FCSTD DOCUMENT  (FreeCAD 0.19R)
Label: nozzle-carriage-v5
License: All rights reserved
LicenseURL: http://en.wikipedia.org/wiki/All_rights_reserved
objects: Sketcher::SketchObject×1, PartDesign::Body×1
note: 2 computed .brp shape members not serialized (recipe doc carries the construction recipe); baked Part::Feature solids carry a one-line shape summary decoded from their .brp

FEATURE [Sketcher::SketchObject] Sketch
  MapMode = 5
  Support = -> [XY_Plane]
  sketch-geometry (28):
    g0: LineSegment StartX=-27.5 StartY=-27.5 StartZ=0 EndX=27.5 EndY=-27.5 EndZ=0
    g1: LineSegment StartX=32.5 StartY=-22.5 StartZ=0 EndX=32.5 EndY=22.5 EndZ=0
    g2: LineSegment StartX=27.5 StartY=27.5 StartZ=0 EndX=-27.5 EndY=27.5 EndZ=0
    g3: LineSegment StartX=-32.5 StartY=22.5 StartZ=0 EndX=-32.5 EndY=-22.5 EndZ=0
    g4: ArcOfCircle CenterX=-27.5 CenterY=22.5 CenterZ=0 NormalX=0 NormalY=0 NormalZ=1 AngleXU=0 Radius=5 StartAngle=1.5708 EndAngle=3.14159
    g5: ArcOfCircle CenterX=27.5 CenterY=22.5 CenterZ=0 NormalX=0 NormalY=0 NormalZ=1 AngleXU=0 Radius=5 StartAngle=2e-16 EndAngle=1.5708
    g6: ArcOfCircle CenterX=27.5 CenterY=-22.5 CenterZ=0 NormalX=0 NormalY=0 NormalZ=1 AngleXU=0 Radius=5 StartAngle=4.71239 EndAngle=6.28319
    g7: ArcOfCircle CenterX=-27.5 CenterY=-22.5 CenterZ=0 NormalX=0 NormalY=0 NormalZ=1 AngleXU=0 Radius=5 StartAngle=3.14159 EndAngle=4.71239
    g8: LineSegment [constr] StartX=-32.5 StartY=20 StartZ=0 EndX=32.5 EndY=20 EndZ=0
    g9: Circle CenterX=-22.5 CenterY=20 CenterZ=0 NormalX=0 NormalY=0 NormalZ=1 AngleXU=0 Radius=3
    g10: Circle CenterX=22.5 CenterY=20 CenterZ=0 NormalX=0 NormalY=0 NormalZ=1 AngleXU=0 Radius=3
    g11: Circle CenterX=0 CenterY=-20 CenterZ=0 NormalX=0 NormalY=0 NormalZ=1 AngleXU=0 Radius=3
    g12: LineSegment [constr] StartX=-32.5 StartY=9.75 StartZ=0 EndX=32.5 EndY=9.75 EndZ=0
    g13: Circle CenterX=-12 CenterY=9.75 CenterZ=0 NormalX=0 NormalY=0 NormalZ=1 AngleXU=0 Radius=1.5
    g14: Circle CenterX=12 CenterY=9.75 CenterZ=0 NormalX=0 NormalY=0 NormalZ=1 AngleXU=0 Radius=1.5
    g15: LineSegment [constr] StartX=-32.5 StartY=-20 StartZ=0 EndX=32.5 EndY=-20 EndZ=0
    g16: Circle CenterX=-20.5 CenterY=-20 CenterZ=0 NormalX=0 NormalY=0 NormalZ=1 AngleXU=0 Radius=1.5
    g17: Circle CenterX=-13.5 CenterY=-20 CenterZ=0 NormalX=0 NormalY=0 NormalZ=1 AngleXU=0 Radius=1.5
    g18: Circle CenterX=-27.5 CenterY=-20 CenterZ=0 NormalX=0 NormalY=0 NormalZ=1 AngleXU=0 Radius=1.5
    g19: Circle CenterX=13.5 CenterY=-20 CenterZ=0 NormalX=0 NormalY=0 NormalZ=1 AngleXU=0 Radius=1.5
    g20: Circle CenterX=20.5 CenterY=-20 CenterZ=0 NormalX=0 NormalY=0 NormalZ=1 AngleXU=0 Radius=1.5
    g21: Circle CenterX=27.5 CenterY=-20 CenterZ=0 NormalX=0 NormalY=0 NormalZ=1 AngleXU=0 Radius=1.5
    g22: LineSegment [constr] StartX=-22.5 StartY=27.5 StartZ=0 EndX=-22.5 EndY=-27.5 EndZ=0
    g23: LineSegment [constr] StartX=22.5 StartY=27.5 StartZ=0 EndX=22.5 EndY=-27.5 EndZ=0
    g24: Circle CenterX=-22.5 CenterY=7.5 CenterZ=0 NormalX=0 NormalY=0 NormalZ=1 AngleXU=0 Radius=1.5
    g25: Circle CenterX=-22.5 CenterY=-7.5 CenterZ=0 NormalX=0 NormalY=0 NormalZ=1 AngleXU=0 Radius=1.5
    g26: Circle CenterX=22.5 CenterY=7.5 CenterZ=0 NormalX=0 NormalY=0 NormalZ=1 AngleXU=0 Radius=1.5
    g27: Circle CenterX=22.5 CenterY=-7.5 CenterZ=0 NormalX=0 NormalY=0 NormalZ=1 AngleXU=0 Radius=1.5
  constraints (84):
    c: Horizontal(g0)
    c: Horizontal(g2)
    c: Vertical(g1)
    c: Vertical(g3)
    c: Tangent(g2,g4) = -1.5708
    c: Tangent(g3,g4) = -1.5708
    c: Tangent(g1,g5) = -1.5708
    c: Tangent(g2,g5) = -1.5708
    c: Tangent(g0,g6) = -1.5708
    c: Tangent(g1,g6) = -1.5708
    c: Tangent(g0,g7) = -1.5708
    c: Tangent(g3,g7) = -1.5708
    c: Symmetric(g4,g6,g-1)
    c: Equal(g4,g7)
    c: Equal(g7,g6)
    c: Equal(g6,g5)
    c: Diameter(g4) = 10
    c: DistanceX(g3,g1) = 65
    c: DistanceY(g0,g2) = 55
    c: PointOnObject(g8,g3)
    c: PointOnObject(g8,g1)
    c: Horizontal(g8)
    c: PointOnObject(g9,g8)
    c: PointOnObject(g10,g8)
    c: PointOnObject(g11,g-2)
    c: Diameter(g9) = 6
    c: DistanceY(g11,g8) = 40
    c: DistanceX(g9,g10) = 45
    c: DistanceY(g-1,g9) = 20
    c: DistanceX(g9,g-1) = 22.5
    c: Equal(g9,g10)
    c: Equal(g10,g11)
    c: PointOnObject(g12,g3)
    c: PointOnObject(g12,g1)
    c: Horizontal(g12)
    c: PointOnObject(g13,g12)
    c: PointOnObject(g14,g12)
    c: Equal(g13,g14)
    c: Diameter(g13) = 3
    c: DistanceX(g13,g14) = 24
    c: DistanceX(g13,g-1) = 12
    c: DistanceY(g-1,g13) = 9.75
    c: PointOnObject(g15,g3)
    c: PointOnObject(g15,g1)
    c: Horizontal(g15)
    c: PointOnObject(g11,g15)
    c: PointOnObject(g16,g15)
    c: PointOnObject(g17,g15)
    c: PointOnObject(g18,g15)
    c: Equal(g18,g16)
    c: Equal(g16,g17)
    c: DistanceX(g18,g17) = 14
    c: DistanceX(g16,g17) = 7
    c: Diameter(g18) = 3
    c: DistanceX(g15,g18) = 5
    c: PointOnObject(g20,g15)
    c: PointOnObject(g21,g15)
    c: Equal(g21,g20)
    c: Equal(g20,g19)
    c: DistanceX(g19,g21) = 14
    c: DistanceX(g20,g21) = 7
    c: Diameter(g19) = 3
    c: DistanceX(g21,g15) = 5
    c: PointOnObject(g22,g2)
    c: PointOnObject(g22,g0)
    c: Vertical(g22)
    c: PointOnObject(g9,g22)
    c: PointOnObject(g23,g2)
    c: PointOnObject(g23,g0)
    c: Vertical(g23)
    c: PointOnObject(g10,g23)
    c: PointOnObject(g19,g15)
    c: PointOnObject(g24,g22)
    c: PointOnObject(g25,g22)
    c: PointOnObject(g26,g23)
    c: PointOnObject(g27,g23)
    c: Equal(g24,g25)
    c: Equal(g25,g26)
    c: Equal(g26,g27)
    c: Diameter(g24) = 3
    c: DistanceY(g25,g24) = 15
    c: DistanceY(g-1,g24) = 7.5
    c: DistanceY(g-1,g26) = 7.5
    c: DistanceY(g27,g26) = 15
FEATURE [PartDesign::Body] Body
  Group = -> [Sketch]
  Origin = -> Origin
